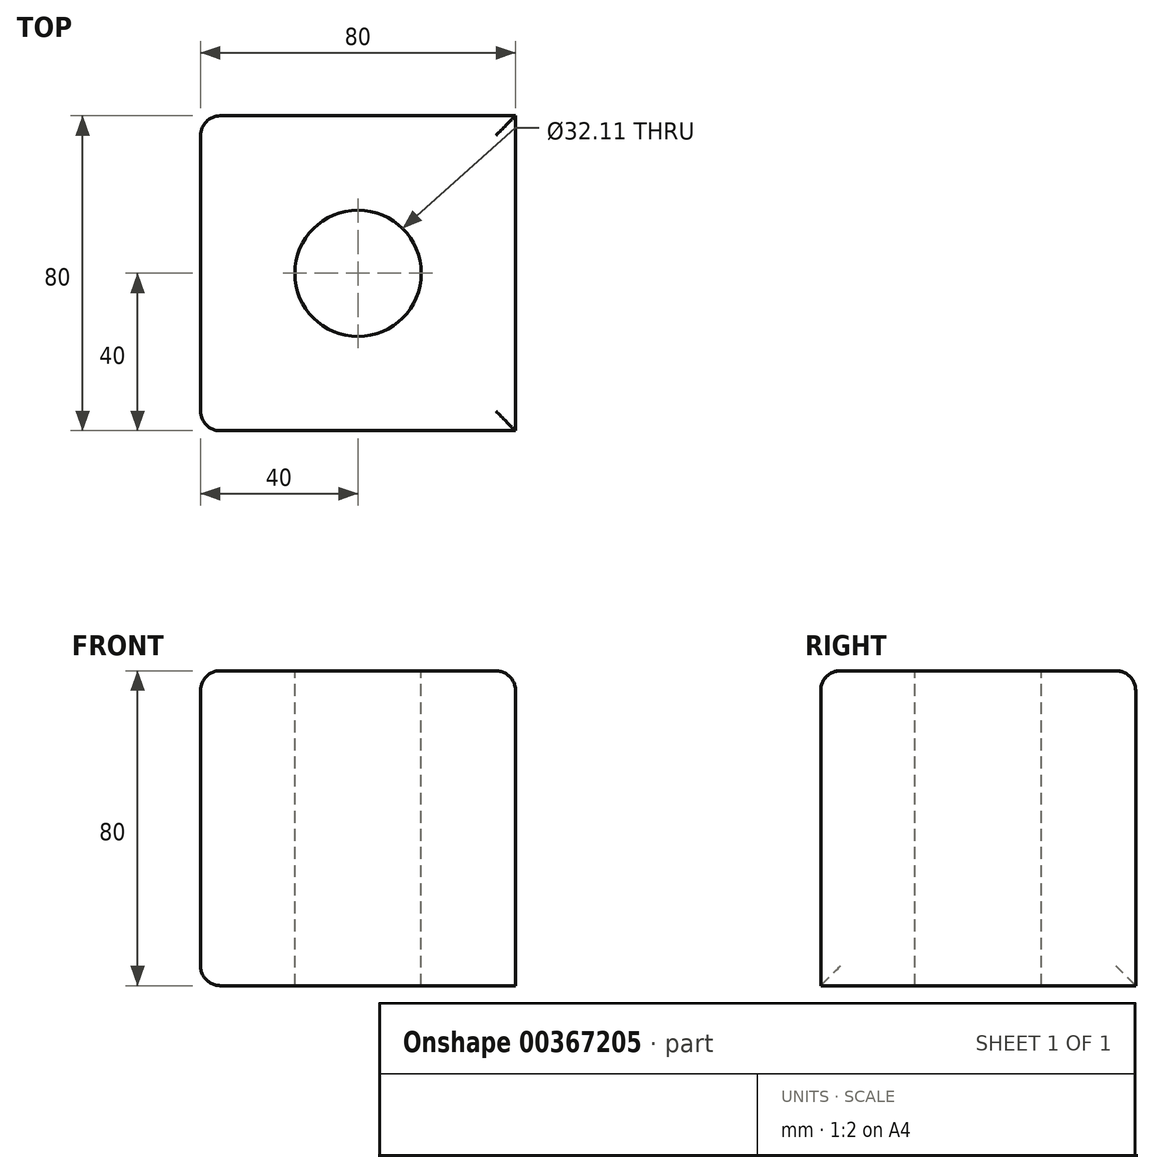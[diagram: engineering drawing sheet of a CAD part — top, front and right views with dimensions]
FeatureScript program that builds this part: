
annotation { "Feature Type Name" : "Feature", "Feature Type Description" : "" }
export const myFeature = defineFeature(function(context is Context, id is Id, definition is map)
    precondition{}
    {
        {
            var Q0;
            Q0=qCreatedBy(makeId("Top.planeOp"),FACE);
            var sketch = newSketch(context, id + "F0", { "sketchPlane" : qUnion([Q0])});
            skLineSegment(sketch, "E0.bottom", {"start": v(-40, 40) * mm, "end": v(40, 40) * mm});
            skLineSegment(sketch, "E0.top", {"start": v(-40, -40) * mm, "end": v(40, -40) * mm});
            skLineSegment(sketch, "E0.left", {"start": v(-40, 40) * mm, "end": v(-40, -40) * mm});
            skLineSegment(sketch, "E0.right", {"start": v(40, 40) * mm, "end": v(40, -40) * mm});
            skPoint(sketch, "E0.middle", {"position": v(0, 0) * mm});
            skSolve(sketch);
        }
        {
            var Q0;
            Q0=makeQuery(id+"F0.imprint","IMPRINT",FACE,{"disambiguationData":[TD([[makeQuery(id+"F0.imprint","IMPRINT",EDGE,{"derivedFrom":sQuery(id+"F0.wireOp",EDGE,"E0.bottom")}),-1.0]])]});
            extrude(context, id + "F1", {"entities" : qUnion([Q0]), "depth" : 80 * mm});
        }
        {
            var Q0;
            Q0=makeQuery(id+"F1.opExtrude","CAP_FACE",FACE,{"disambiguationData":[OSD([sQuery(id+"F0.wireOp",EDGE,"E0.bottom"),sQuery(id+"F0.wireOp",EDGE,"E0.top"),sQuery(id+"F0.wireOp",EDGE,"E0.left"),sQuery(id+"F0.wireOp",EDGE,"E0.right")])],"isStart":false});
            var sketch = newSketch(context, id + "F2", { "sketchPlane" : qUnion([Q0])});
            skCircle(sketch, "E1", {"center": v(0, 0) * mm, "radius": 16.06 * mm});
            skSolve(sketch);
        }
        {
            var Q0;
            Q0=makeQuery(id+"F2.imprint","IMPRINT",FACE,{"disambiguationData":[TD([[makeQuery(id+"F2.imprint","IMPRINT",EDGE,{"derivedFrom":sQuery(id+"F2.wireOp",EDGE,"E1")}),1.0]])]});
            extrude(context, id + "F3", {"entities" : qUnion([Q0]), "operationType" : NewBodyOperationType.REMOVE, "endBound" : BoundingType.THROUGH_ALL, "oppositeDirection" : true, "depth" : 25 * mm});
        }
        {
            var Q0;
            Q0=makeQuery(id+"F1.opExtrude","CAP_EDGE",EDGE,{"disambiguationData":[OSD([sQuery(id+"F0.wireOp",EDGE,"E0.bottom")])],"isStart":false});
            var Q1;
            Q1=makeQuery(id+"F1.opExtrude","CAP_EDGE",EDGE,{"disambiguationData":[OSD([sQuery(id+"F0.wireOp",EDGE,"E0.left")])],"isStart":false});
            var Q2;
            Q2=makeQuery(id+"F1.opExtrude","CAP_EDGE",EDGE,{"disambiguationData":[OSD([sQuery(id+"F0.wireOp",EDGE,"E0.top")])],"isStart":false});
            var Q3;
            Q3=makeQuery(id+"F1.opExtrude","CAP_EDGE",EDGE,{"disambiguationData":[OSD([sQuery(id+"F0.wireOp",EDGE,"E0.right")])],"isStart":false});
            var Q4;
            Q4=makeQuery(id+"F1.opExtrude","SWEPT_EDGE",EDGE,{"disambiguationData":[OSD([sQuery(id+"F0.wireOp",EDGE,"E0.bottom"),sQuery(id+"F0.wireOp",EDGE,"E0.left")])]});
            var Q5;
            Q5=makeQuery(id+"F1.opExtrude","SWEPT_FACE",FACE,{"disambiguationData":[OSD([sQuery(id+"F0.wireOp",EDGE,"E0.left")])]});
            var Q6;
            Q6=makeQuery(id+"F1.opExtrude","SWEPT_EDGE",EDGE,{"disambiguationData":[OSD([sQuery(id+"F0.wireOp",EDGE,"E0.top"),sQuery(id+"F0.wireOp",EDGE,"E0.left")])]});
            fillet(context, id + "F4", {"entities" : qUnion([Q0, Q1, Q2, Q3, Q4, Q5, Q6]), "radius" : 5 * mm, "tangentPropagation" : true, "allowEdgeOverflow" : false});
        }
    });
